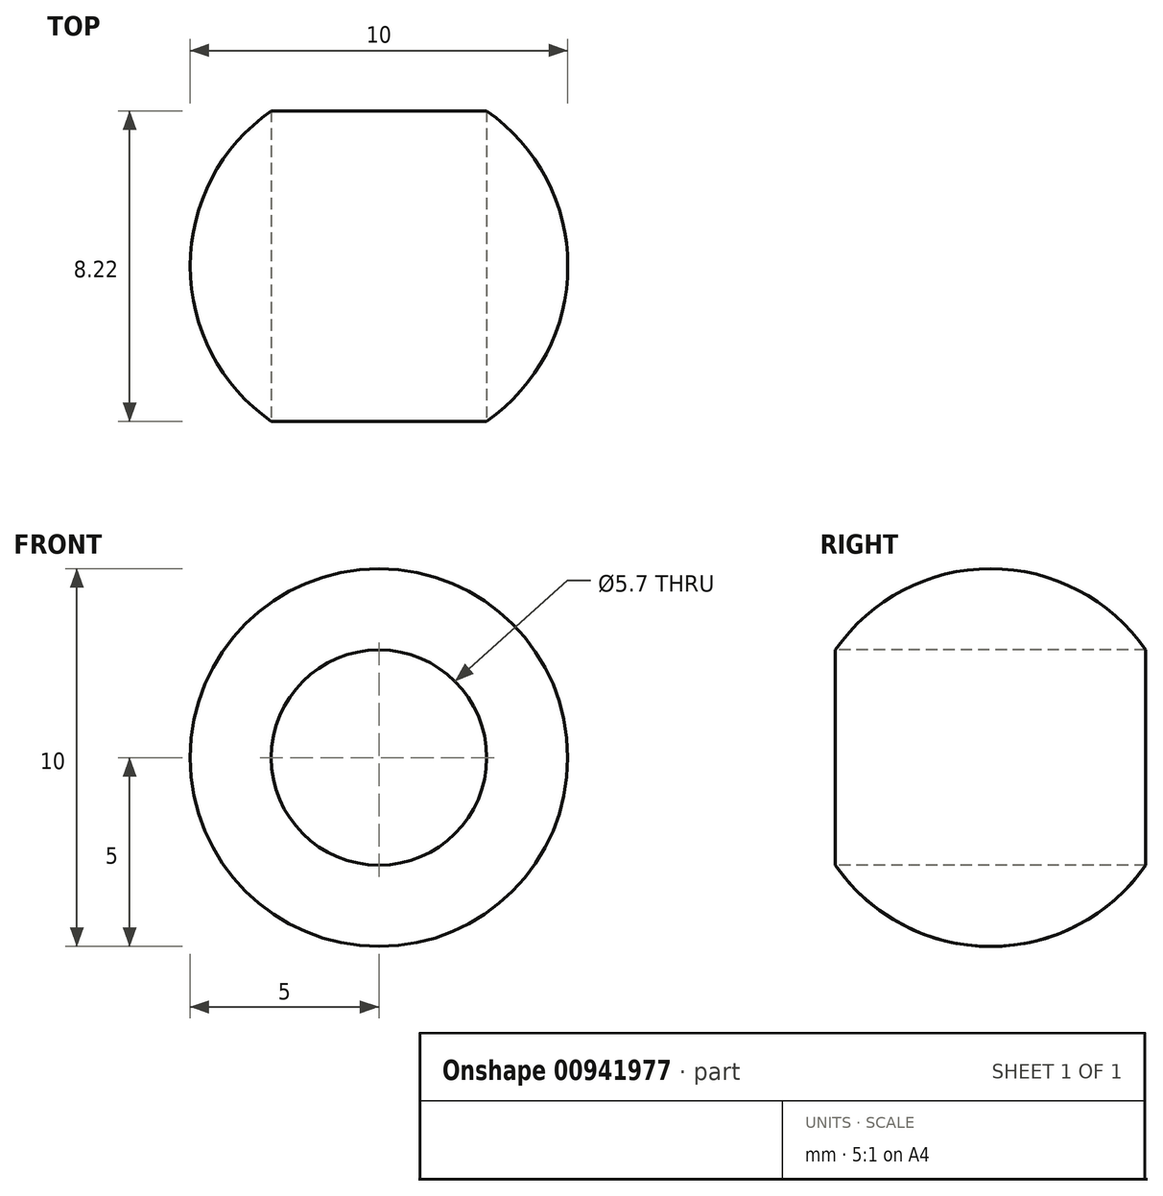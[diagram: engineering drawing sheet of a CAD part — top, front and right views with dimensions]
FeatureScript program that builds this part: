
annotation { "Feature Type Name" : "Feature", "Feature Type Description" : "" }
export const myFeature = defineFeature(function(context is Context, id is Id, definition is map)
    precondition{}
    {
        {
            var Q0;
            Q0=qCreatedBy(makeId("Top.planeOp"),FACE);
            var sketch = newSketch(context, id + "F0", { "sketchPlane" : qUnion([Q0])});
            skLineSegment(sketch, "E0", {"start": v(0, 0) * mm, "end": v(0, 10) * mm});
            skArc(sketch, "E1", {"start": v(0, 10) * mm, "mid": v(5, 5) * mm, "end": v(0, 0) * mm});
            skLineSegment(sketch, "E2", {"start": v(2.85, 9.1) * mm, "end": v(2.85, 0.9) * mm});
            skSolve(sketch);
        }
        {
            var Q0;
            {var subQ0=sQuery(id+"F0.wireOp",EDGE,"E2");Q0=makeQuery(id+"F0.imprint","IMPRINT",FACE,{"disambiguationData":[TD([[makeQuery(id+"F0.imprint","IMPRINT",EDGE,{"derivedFrom":subQ0}),1.0]])]});}
            var Q1;
            Q1=sQuery(id+"F0.wireOp",EDGE,"E0");
            revolve(context, id + "F1", {"surfaceOperationType" : NewSurfaceOperationType.NEW, "entities" : qUnion([Q0]), "axis" : qUnion([Q1]), "revolveType" : RevolveType.FULL});
        }
    });
